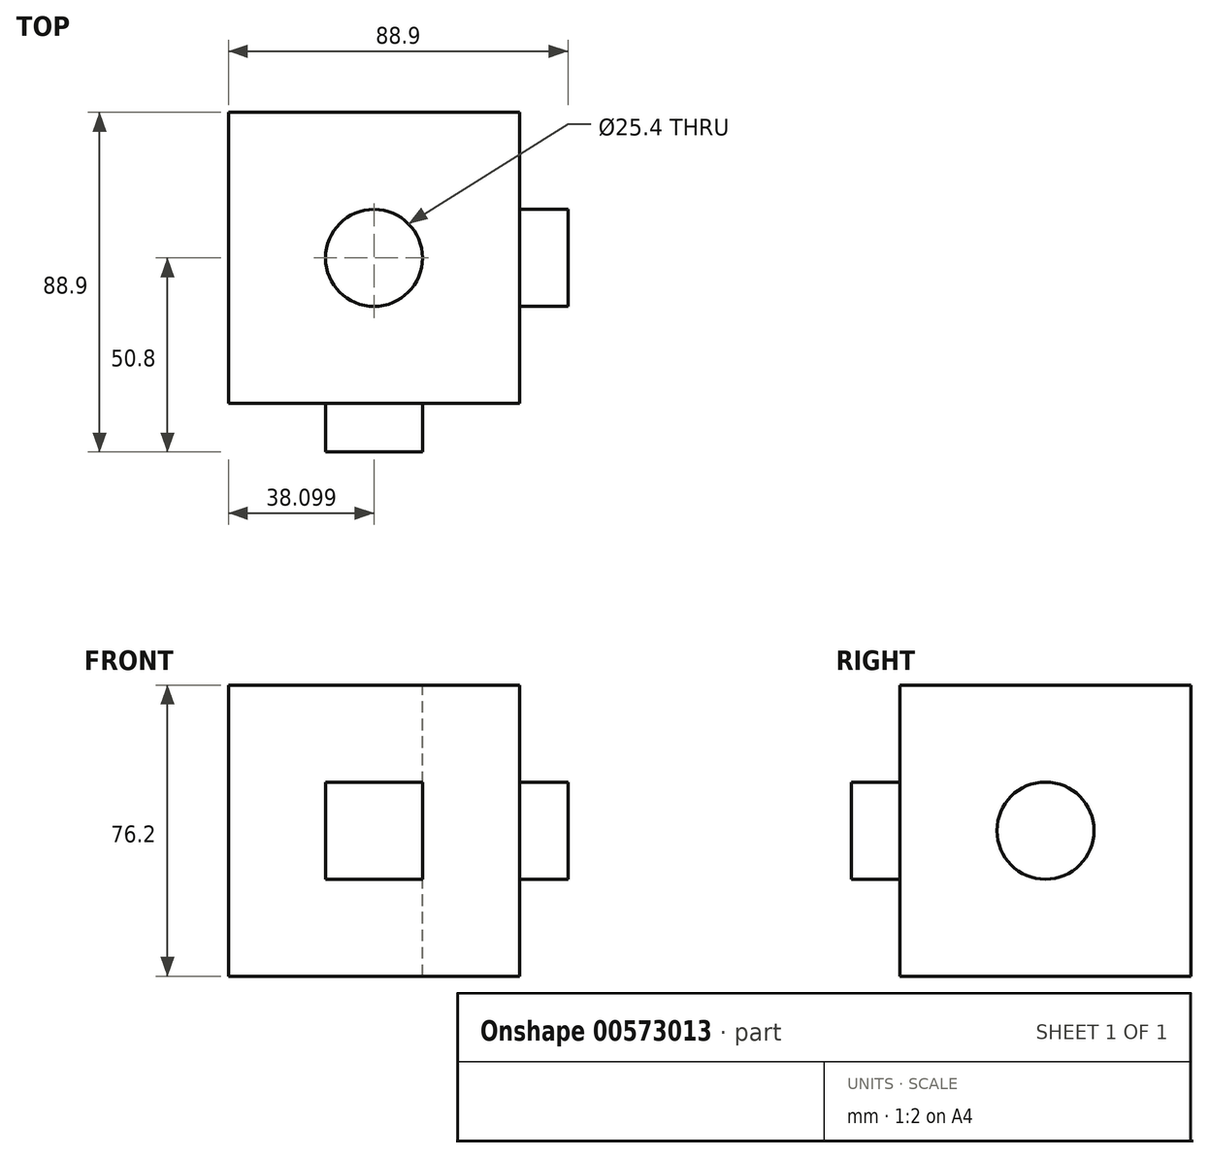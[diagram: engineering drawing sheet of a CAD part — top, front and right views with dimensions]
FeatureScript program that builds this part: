
annotation { "Feature Type Name" : "Feature", "Feature Type Description" : "" }
export const myFeature = defineFeature(function(context is Context, id is Id, definition is map)
    precondition{}
    {
        {
            var Q0;
            Q0=qCreatedBy(makeId("Front.planeOp"),FACE);
            var sketch = newSketch(context, id + "F0", { "sketchPlane" : qUnion([Q0])});
            skLineSegment(sketch, "E0.bottom", {"start": v(-37.72, -31.12) * mm, "end": v(38.48, -31.12) * mm});
            skLineSegment(sketch, "E0.top", {"start": v(-37.72, 45.08) * mm, "end": v(38.48, 45.08) * mm});
            skLineSegment(sketch, "E0.left", {"start": v(-37.72, -31.12) * mm, "end": v(-37.72, 45.08) * mm});
            skLineSegment(sketch, "E0.right", {"start": v(38.48, -31.12) * mm, "end": v(38.48, 45.08) * mm});
            skSolve(sketch);
        }
        {
            var Q0;
            Q0=makeQuery(id+"F0.imprint","IMPRINT",FACE,{"disambiguationData":[TD([[makeQuery(id+"F0.imprint","IMPRINT",EDGE,{"derivedFrom":sQuery(id+"F0.wireOp",EDGE,"E0.bottom")}),1.0]])]});
            extrude(context, id + "F1", {"entities" : qUnion([Q0]), "oppositeDirection" : true, "depth" : 76.2 * mm, "offsetDistance" : 25.4 * mm});
        }
        {
            var Q0;
            Q0=qCreatedBy(makeId("Front.planeOp"),FACE);
            var sketch = newSketch(context, id + "F2", { "sketchPlane" : qUnion([Q0])});
            skLineSegment(sketch, "E1.bottom", {"start": v(-12.32, 19.68) * mm, "end": v(13.08, 19.68) * mm});
            skLineSegment(sketch, "E1.top", {"start": v(-12.32, -5.72) * mm, "end": v(13.08, -5.72) * mm});
            skLineSegment(sketch, "E1.left", {"start": v(-12.32, 19.68) * mm, "end": v(-12.32, -5.72) * mm});
            skLineSegment(sketch, "E1.right", {"start": v(13.08, 19.68) * mm, "end": v(13.08, -5.72) * mm});
            skSolve(sketch);
        }
        {
            var Q0;
            Q0=makeQuery(id+"F2.imprint","IMPRINT",FACE,{"disambiguationData":[TD([[makeQuery(id+"F2.imprint","IMPRINT",EDGE,{"derivedFrom":sQuery(id+"F2.wireOp",EDGE,"E1.bottom")}),-1.0]])]});
            extrude(context, id + "F3", {"entities" : qUnion([Q0]), "operationType" : NewBodyOperationType.ADD, "depth" : 12.7 * mm, "offsetDistance" : 25.4 * mm});
        }
        {
            var Q0;
            Q0=makeQuery(id+"F1.opExtrude","SWEPT_FACE",FACE,{"disambiguationData":[OSD([sQuery(id+"F0.wireOp",EDGE,"E0.right")])]});
            var sketch = newSketch(context, id + "F4", { "sketchPlane" : qUnion([Q0])});
            skCircle(sketch, "E2", {"center": v(38.1, 6.98) * mm, "radius": 12.7 * mm});
            skSolve(sketch);
        }
        {
            var Q0;
            Q0=makeQuery(id+"F4.imprint","IMPRINT",FACE,{"disambiguationData":[TD([[makeQuery(id+"F4.imprint","IMPRINT",EDGE,{"derivedFrom":sQuery(id+"F4.wireOp",EDGE,"E2")}),1.0]])]});
            extrude(context, id + "F5", {"entities" : qUnion([Q0]), "operationType" : NewBodyOperationType.ADD, "depth" : 12.7 * mm, "offsetDistance" : 25.4 * mm});
        }
        {
            var Q0;
            Q0=makeQuery(id+"F1.opExtrude","SWEPT_FACE",FACE,{"disambiguationData":[OSD([sQuery(id+"F0.wireOp",EDGE,"E0.top")])]});
            var sketch = newSketch(context, id + "F6", { "sketchPlane" : qUnion([Q0])});
            skPoint(sketch, "E3", {"position": v(0.38, 38.1) * mm});
            skSolve(sketch);
        }
        {
            var Q0;
            Q0=sQuery(id+"F6.wireOp",VERTEX,"E3");
            var Q1;
            Q1=makeQuery(id+"F1.opExtrude","SWEPT_BODY",BODY,{"disambiguationData":[OSD([sQuery(id+"F0.wireOp",EDGE,"E0.bottom"),sQuery(id+"F0.wireOp",EDGE,"E0.top"),sQuery(id+"F0.wireOp",EDGE,"E0.left"),sQuery(id+"F0.wireOp",EDGE,"E0.right")])]});
            hole(context, id + "F7", {"style" : HoleStyle.SIMPLE, "endStyle" : HoleEndStyle.THROUGH, "holeDiameter" : 25.4 * mm, "isTappedThrough" : true, "tappedDepth" : 12.7 * mm, "tapClearance" : 3, "locations" : qUnion([Q0]), "scope" : qUnion([Q1])});
        }
    });
